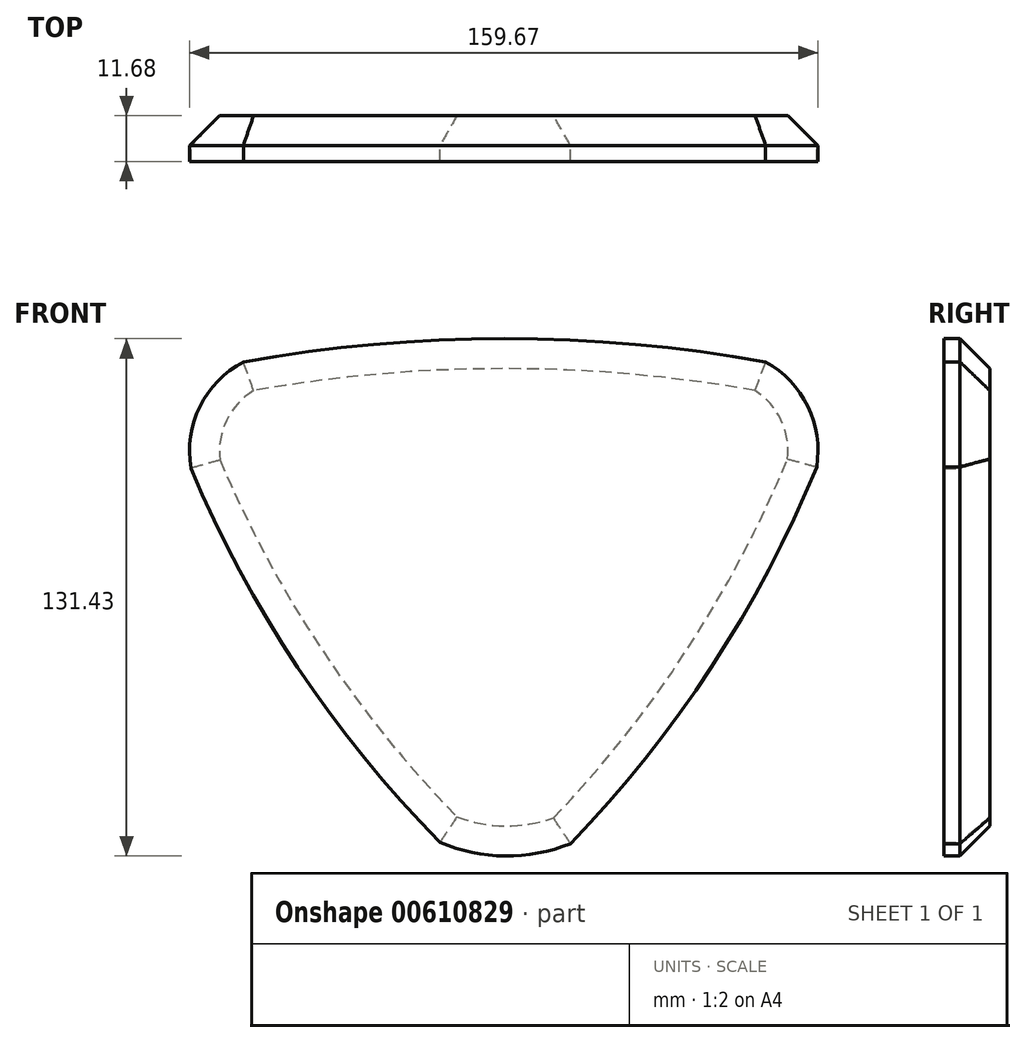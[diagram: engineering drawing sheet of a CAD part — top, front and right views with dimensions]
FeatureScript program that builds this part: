
annotation { "Feature Type Name" : "Feature", "Feature Type Description" : "" }
export const myFeature = defineFeature(function(context is Context, id is Id, definition is map)
    precondition{}
    {
        {
            var Q0;
            Q0=qCreatedBy(makeId("Front.planeOp"),FACE);
            var sketch = newSketch(context, id + "F0", { "sketchPlane" : qUnion([Q0])});
            skArc(sketch, "E0", {"start": v(66.33, 56.57) * mm, "mid": v(0, 62.5) * mm, "end": v(-66.32, 56.57) * mm});
            skArc(sketch, "E1", {"start": v(16.75, -65.82) * mm, "mid": v(52.58, -20.93) * mm, "end": v(79.32, 29.9) * mm});
            skArc(sketch, "E2", {"start": v(-79.66, 29.56) * mm, "mid": v(-52.6, -21) * mm, "end": v(-16.4, -65.48) * mm});
            skArc(sketch, "E3", {"start": v(79.32, 29.9) * mm, "mid": v(77.03, 45.29) * mm, "end": v(66.33, 56.57) * mm});
            skArc(sketch, "E4", {"start": v(-66.32, 56.57) * mm, "mid": v(-77.39, 45.23) * mm, "end": v(-79.66, 29.56) * mm});
            skArc(sketch, "E5", {"start": v(-16.4, -65.48) * mm, "mid": v(0.14, -68.94) * mm, "end": v(16.75, -65.82) * mm});
            skSolve(sketch);
        }
        {
            var Q0;
            Q0 = qSketchRegion(id + "F0", true);
            extrude(context, id + "F1", {"entities" : qUnion([Q0]), "depth" : 11.68 * mm, "offsetDistance" : 25.4 * mm});
        }
        {
            var Q0;
            Q0=makeQuery(id+"F1.opExtrude","CAP_FACE",FACE,{"disambiguationData":[OSD([sQuery(id+"F0.wireOp",EDGE,"E0"),sQuery(id+"F0.wireOp",EDGE,"E1"),sQuery(id+"F0.wireOp",EDGE,"E2"),sQuery(id+"F0.wireOp",EDGE,"E3"),sQuery(id+"F0.wireOp",EDGE,"E4"),sQuery(id+"F0.wireOp",EDGE,"E5")])],"isStart":true});
            chamfer(context, id + "F2", {"entities" : qUnion([Q0]), "width" : 7.62 * mm, "tangentPropagation" : true});
        }
    });
